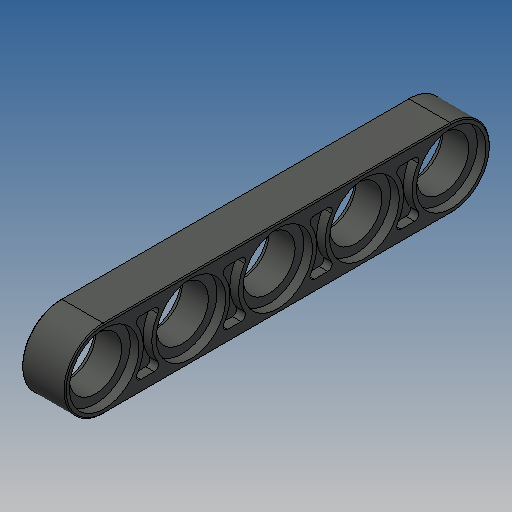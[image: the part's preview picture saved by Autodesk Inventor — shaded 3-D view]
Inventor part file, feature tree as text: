
AUTODESK INVENTOR PART (.ipt)
format: ipt  version: 2025 (Build 290162010, 162A)  size: 308,736 bytes
history: native  units: mm
features: extrude x3, sketch x3, mirror x1, fillet x1
ambient origin geometry x8: Origin, YZ Plane, XZ Plane, XY Plane, X Axis, Y Axis, Z Axis, Center Point
bodies: Solid1 (feature_tree)
feature tree (8):
  extrude  "Extrusion4"  Depth=7.2mm
  sketch  "Sketch11"  dims[d60=4.8mm d61=6.4mm d62=0.8mm d63=0.0mm d64=8.0mm d65=45.0deg d66=40.0mm d68=8.0mm d69=10.0mm d71=10.0mm d73=0.8mm d74=0.0mm d75=0.4mm]
  extrude  "Extrusion16"  Depth=0.1mm
  extrude  "Extrusion17"  Depth=0.4mm
  mirror  "Mirror3"
  fillet  "Fillet1"  Radius=0.8mm
  sketch  "Sketch3"  dims[d56=0.1mm d59=6.4mm]
  sketch  "Skizze - Rechteckige Anordnung1"  dims[d15=4.0mm d16=0.0mm d49=7.2mm]
